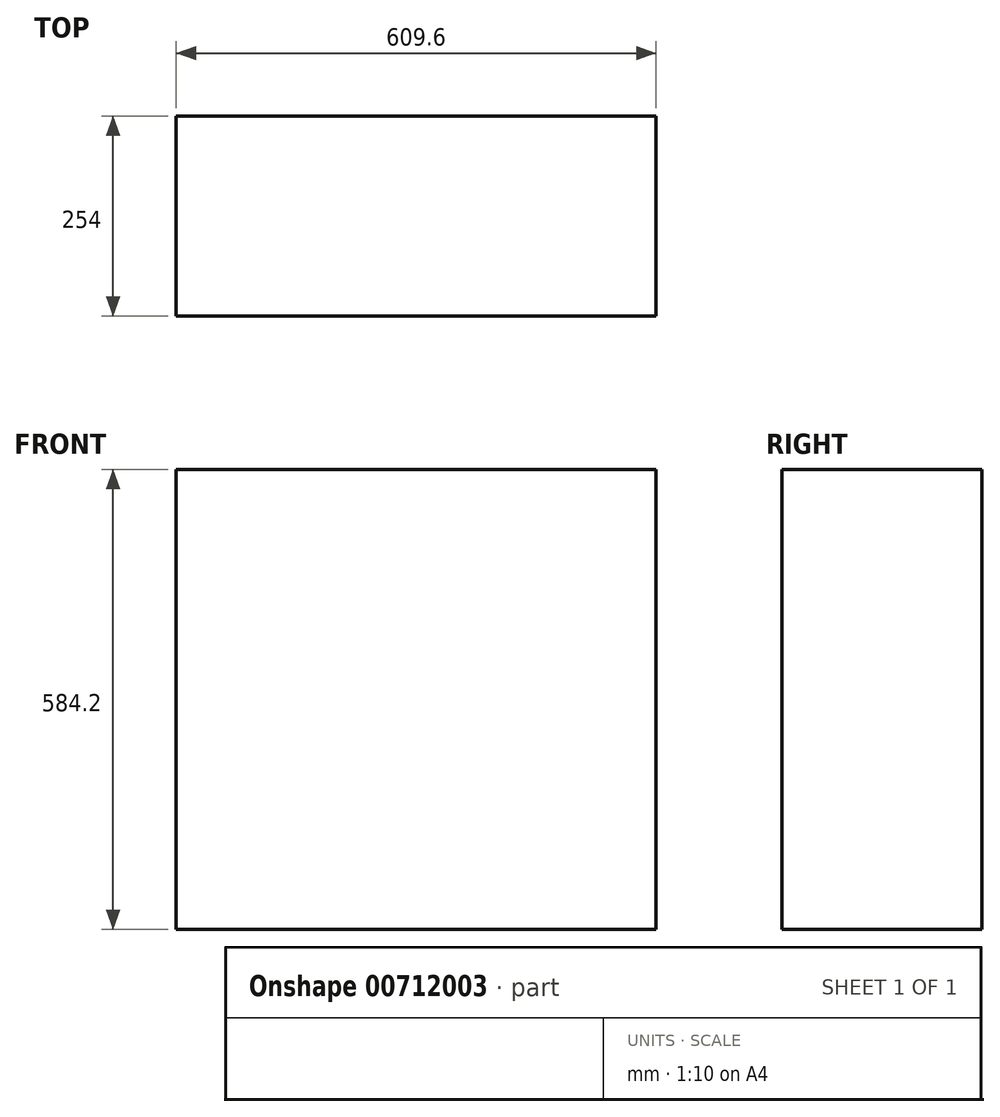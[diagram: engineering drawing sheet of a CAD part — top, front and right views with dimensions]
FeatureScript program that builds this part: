
annotation { "Feature Type Name" : "Feature", "Feature Type Description" : "" }
export const myFeature = defineFeature(function(context is Context, id is Id, definition is map)
    precondition{}
    {
        {
            var Q0;
            Q0=qCreatedBy(makeId("Front.planeOp"),FACE);
            var sketch = newSketch(context, id + "F0", { "sketchPlane" : qUnion([Q0])});
            skLineSegment(sketch, "E0.bottom", {"start": v(-288.1, 308.21) * mm, "end": v(321.5, 308.21) * mm});
            skLineSegment(sketch, "E0.top", {"start": v(-288.1, -275.99) * mm, "end": v(321.5, -275.99) * mm});
            skLineSegment(sketch, "E0.left", {"start": v(-288.1, 308.21) * mm, "end": v(-288.1, -275.99) * mm});
            skLineSegment(sketch, "E0.right", {"start": v(321.5, 308.21) * mm, "end": v(321.5, -275.99) * mm});
            skLineSegment(sketch, "E1.bottom", {"start": v(-220.04, 244.9) * mm, "end": v(262.7, 244.9) * mm});
            skLineSegment(sketch, "E1.top", {"start": v(-220.04, -228.7) * mm, "end": v(262.7, -228.7) * mm});
            skLineSegment(sketch, "E1.left", {"start": v(-220.04, 244.9) * mm, "end": v(-220.04, -228.7) * mm});
            skLineSegment(sketch, "E1.right", {"start": v(262.7, 244.9) * mm, "end": v(262.7, -228.7) * mm});
            skSolve(sketch);
        }
        {
            var Q0;
            Q0=makeQuery(id+"F0.imprint","IMPRINT",FACE,{"disambiguationData":[TD([[makeQuery(id+"F0.imprint","IMPRINT",EDGE,{"derivedFrom":sQuery(id+"F0.wireOp",EDGE,"E0.bottom")}),-1.0]])]});
            var Q1;
            Q1=makeQuery(id+"F0.imprint","IMPRINT",FACE,{"disambiguationData":[TD([[makeQuery(id+"F0.imprint","IMPRINT",EDGE,{"derivedFrom":sQuery(id+"F0.wireOp",EDGE,"E1.bottom")}),-1.0]])]});
            extrude(context, id + "F1", {"entities" : qUnion([Q0, Q1]), "oppositeDirection" : true, "depth" : 254 * mm, "offsetDistance" : 25.4 * mm});
        }
    });
